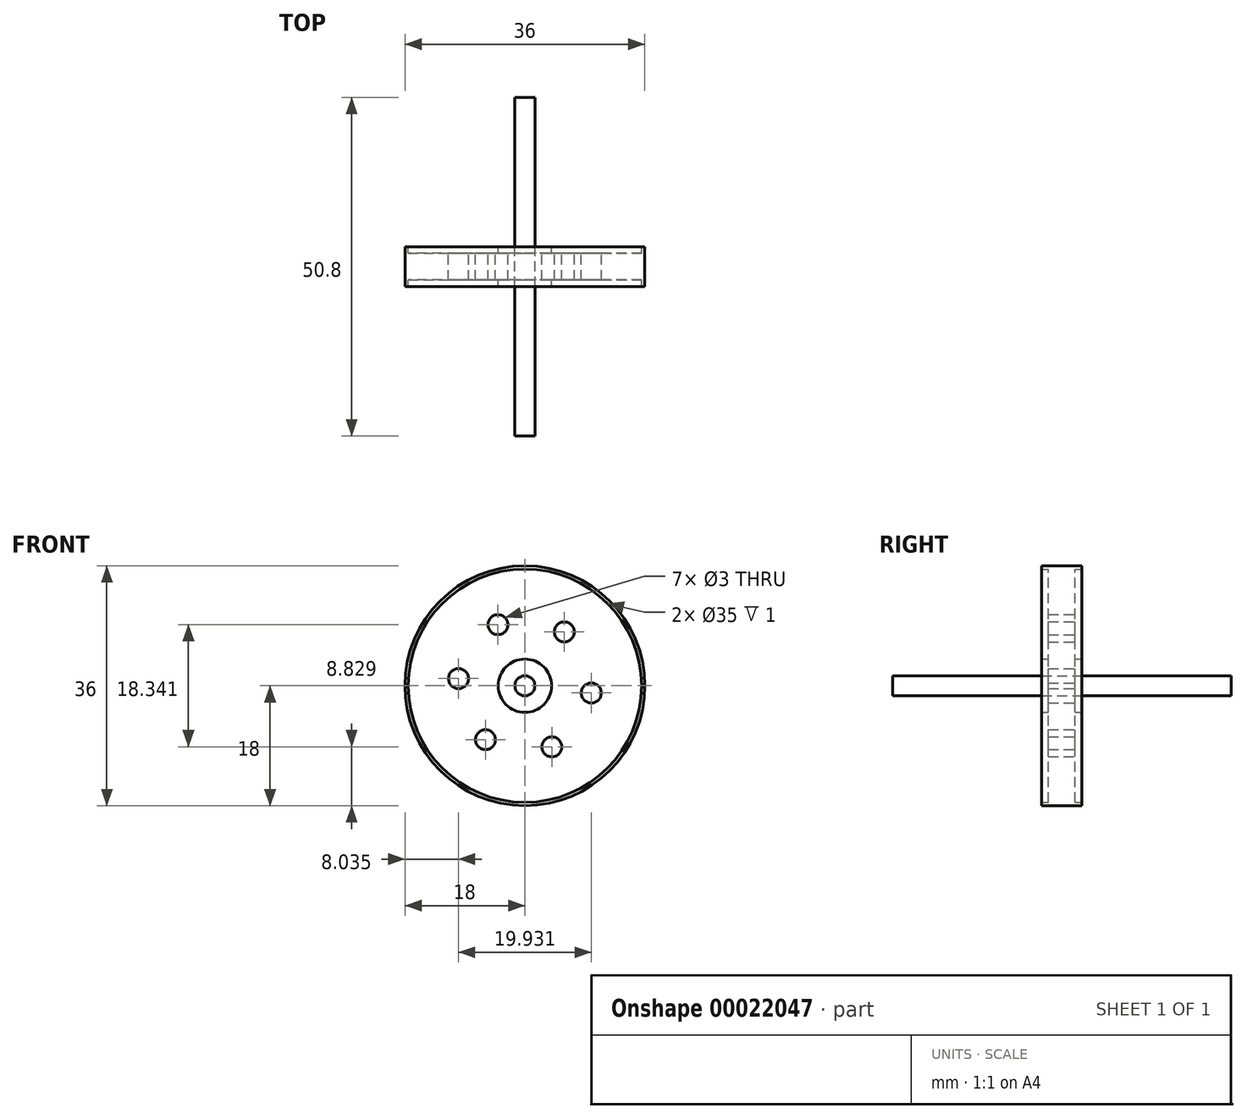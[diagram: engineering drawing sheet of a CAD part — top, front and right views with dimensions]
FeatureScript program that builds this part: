
annotation { "Feature Type Name" : "Feature", "Feature Type Description" : "" }
export const myFeature = defineFeature(function(context is Context, id is Id, definition is map)
    precondition{}
    {
        {
            var Q0;
            Q0=qCreatedBy(makeId("Front.planeOp"),FACE);
            var sketch = newSketch(context, id + "F0", { "sketchPlane" : qUnion([Q0])});
            skCircle(sketch, "E0", {"center": v(0, 0) * mm, "radius": 17.5 * mm});
            skCircle(sketch, "E1", {"center": v(0, 0) * mm, "radius": 4 * mm});
            skCircle(sketch, "E2", {"center": v(0, 0) * mm, "radius": 1.5 * mm});
            skCircle(sketch, "E3", {"center": v(-9.97, 1.08) * mm, "radius": 1.5 * mm});
            skLineSegment(sketch, "E4", {"start": v(-11.47, 1.1) * mm, "end": v(-17.47, 1.1) * mm});
            skCircle(sketch, "E5.1.0", {"center": v(-5.92, -8.09) * mm, "radius": 1.5 * mm});
            skCircle(sketch, "E5.2.0", {"center": v(4.05, -9.17) * mm, "radius": 1.5 * mm});
            skCircle(sketch, "E5.3.0", {"center": v(9.97, -1.08) * mm, "radius": 1.5 * mm});
            skCircle(sketch, "E5.4.0", {"center": v(5.92, 8.09) * mm, "radius": 1.5 * mm});
            skCircle(sketch, "E5.5.0", {"center": v(-4.05, 9.17) * mm, "radius": 1.5 * mm});
            skCircle(sketch, "E6", {"center": v(0, 0) * mm, "radius": 18 * mm});
            skSolve(sketch);
        }
        {
            var Q0;
            Q0=makeQuery(id+"F0.imprint","IMPRINT",FACE,{"disambiguationData":[TD([[makeQuery(id+"F0.imprint","IMPRINT",EDGE,{"derivedFrom":sQuery(id+"F0.wireOp",EDGE,"E0")}),1.0]])]});
            extrude(context, id + "F1", {"entities" : qUnion([Q0]), "endBound" : BoundingType.SYMMETRIC, "depth" : 4 * mm});
        }
        {
            var Q0;
            Q0=makeQuery(id+"F0.imprint","IMPRINT",FACE,{"disambiguationData":[TD([[makeQuery(id+"F0.imprint","IMPRINT",EDGE,{"derivedFrom":sQuery(id+"F0.wireOp",EDGE,"E1")}),1.0]])]});
            extrude(context, id + "F2", {"entities" : qUnion([Q0]), "operationType" : NewBodyOperationType.ADD, "endBound" : BoundingType.SYMMETRIC, "depth" : 6 * mm});
        }
        {
            var Q0;
            Q0=makeQuery(id+"F0.imprint","IMPRINT",FACE,{"disambiguationData":[TD([[makeQuery(id+"F0.imprint","IMPRINT",EDGE,{"derivedFrom":sQuery(id+"F0.wireOp",EDGE,"E0")}),-1.0]])]});
            extrude(context, id + "F3", {"entities" : qUnion([Q0]), "operationType" : NewBodyOperationType.ADD, "endBound" : BoundingType.SYMMETRIC, "depth" : 6 * mm});
        }
        {
            var Q0;
            Q0=makeQuery(id+"F0.imprint","IMPRINT",FACE,{"disambiguationData":[TD([[makeQuery(id+"F0.imprint","IMPRINT",EDGE,{"derivedFrom":sQuery(id+"F0.wireOp",EDGE,"E2")}),1.0]])]});
            extrude(context, id + "F4", {"entities" : qUnion([Q0]), "endBound" : BoundingType.SYMMETRIC, "depth" : 50.8 * mm});
        }
    });
